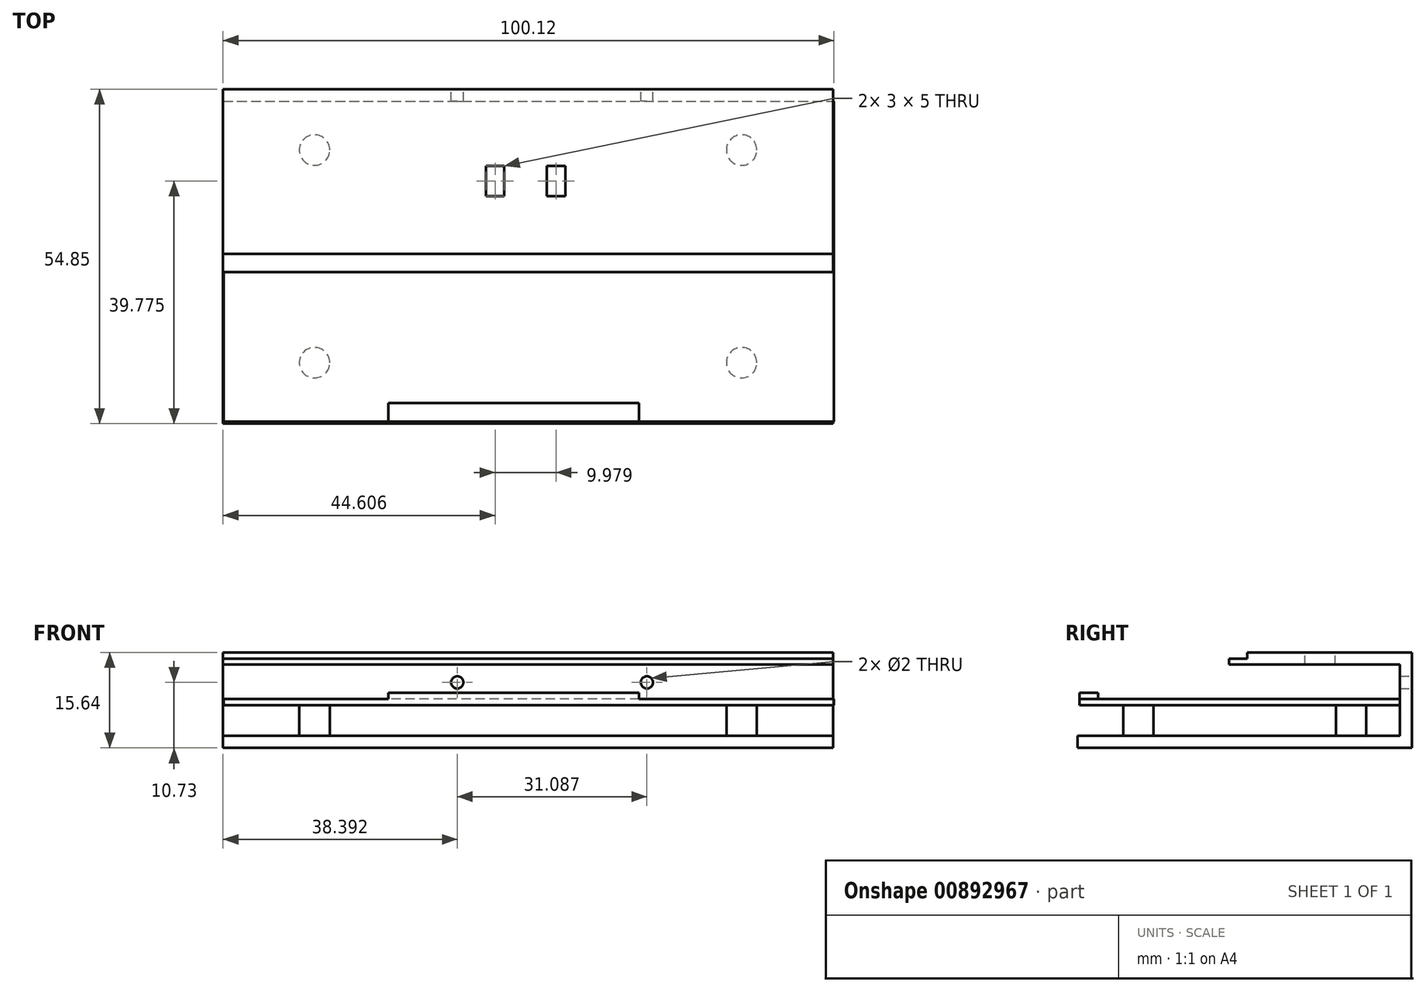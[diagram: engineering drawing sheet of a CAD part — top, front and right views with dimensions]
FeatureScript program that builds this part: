
annotation { "Feature Type Name" : "Feature", "Feature Type Description" : "" }
export const myFeature = defineFeature(function(context is Context, id is Id, definition is map)
    precondition{}
    {
        {
            var Q0;
            Q0=qCreatedBy(makeId("Right.planeOp"),FACE);
            var sketch = newSketch(context, id + "F0", { "sketchPlane" : qUnion([Q0])});
            skLineSegment(sketch, "E0", {"start": v(-52.85, 0) * mm, "end": v(0, 0) * mm});
            skLineSegment(sketch, "E1", {"start": v(0, 0) * mm, "end": v(0, 13.64) * mm});
            skLineSegment(sketch, "E2.0", {"start": v(2, -2) * mm, "end": v(2, 13.64) * mm});
            skLineSegment(sketch, "E2.1", {"start": v(-52.85, -2) * mm, "end": v(2, -2) * mm});
            skLineSegment(sketch, "E3.bottom", {"start": v(-52.85, -2) * mm, "end": v(-52.85, -2) * mm});
            skLineSegment(sketch, "E3.top", {"start": v(-52.85, 0) * mm, "end": v(-52.85, 0) * mm});
            skLineSegment(sketch, "E3.left", {"start": v(-52.85, -2) * mm, "end": v(-52.85, 0) * mm});
            skLineSegment(sketch, "E3.right", {"start": v(-52.85, -2) * mm, "end": v(-52.85, 0) * mm});
            skLineSegment(sketch, "E4.bottom", {"start": v(0, 13.64) * mm, "end": v(2, 13.64) * mm});
            skLineSegment(sketch, "E4.top", {"start": v(0, 13.64) * mm, "end": v(2, 13.64) * mm});
            skLineSegment(sketch, "E4.left", {"start": v(0, 13.64) * mm, "end": v(0, 13.64) * mm});
            skLineSegment(sketch, "E4.right", {"start": v(2, 13.64) * mm, "end": v(2, 13.64) * mm});
            skSolve(sketch);
        }
        {
            var Q0;
            Q0=makeQuery(id+"F0.imprint","IMPRINT",FACE,{"disambiguationData":[TD([[makeQuery(id+"F0.imprint","IMPRINT",EDGE,{"derivedFrom":sQuery(id+"F0.wireOp",EDGE,"E0")}),-1.0]])]});
            extrude(context, id + "F1", {"entities" : qUnion([Q0]), "depth" : 100 * mm, "offsetDistance" : 25 * mm});
        }
        {
            var Q0;
            Q0=makeQuery(id+"F1.opExtrude","SWEPT_FACE",FACE,{"disambiguationData":[OSD([sQuery(id+"F0.wireOp",EDGE,"E1")])]});
            var sketch = newSketch(context, id + "F2", { "sketchPlane" : qUnion([Q0])});
            skLineSegment(sketch, "E5.bottom", {"start": v(0, 13.64) * mm, "end": v(100, 13.64) * mm});
            skLineSegment(sketch, "E5.top", {"start": v(0, 11.64) * mm, "end": v(100, 11.64) * mm});
            skLineSegment(sketch, "E5.left", {"start": v(0, 13.64) * mm, "end": v(0, 11.64) * mm});
            skLineSegment(sketch, "E5.right", {"start": v(100, 13.64) * mm, "end": v(100, 11.64) * mm});
            skSolve(sketch);
        }
        {
            var Q0;
            Q0=makeQuery(id+"F2.imprint","IMPRINT",FACE,{"disambiguationData":[TD([[makeQuery(id+"F2.imprint","IMPRINT",EDGE,{"derivedFrom":sQuery(id+"F2.wireOp",EDGE,"E5.bottom")}),1.0]])]});
            extrude(context, id + "F3", {"entities" : qUnion([Q0]), "operationType" : NewBodyOperationType.ADD, "depth" : 25 * mm, "offsetDistance" : 25 * mm});
        }
        {
            var Q0;
            Q0=makeQuery(id+"F1.opExtrude","SWEPT_FACE",FACE,{"disambiguationData":[OSD([sQuery(id+"F0.wireOp",EDGE,"E0")])]});
            var sketch = newSketch(context, id + "F4", { "sketchPlane" : qUnion([Q0])});
            skCircle(sketch, "E6", {"center": v(15, -42.85) * mm, "radius": 2.5 * mm});
            skCircle(sketch, "E7", {"center": v(85, -42.85) * mm, "radius": 2.5 * mm});
            skCircle(sketch, "E8", {"center": v(15, -8) * mm, "radius": 2.5 * mm});
            skCircle(sketch, "E9", {"center": v(85, -8) * mm, "radius": 2.5 * mm});
            skLineSegment(sketch, "E10", {"start": v(0, -8) * mm, "end": v(100, -8) * mm, "construction": true});
            skLineSegment(sketch, "E11", {"start": v(0, -42.85) * mm, "end": v(100, -42.85) * mm, "construction": true});
            skLineSegment(sketch, "E12", {"start": v(15, 1.66) * mm, "end": v(15, -52.85) * mm, "construction": true});
            skLineSegment(sketch, "E13", {"start": v(85, 2.16) * mm, "end": v(85, -52.85) * mm, "construction": true});
            skSolve(sketch);
        }
        {
            var Q0;
            Q0=makeQuery(id+"F4.imprint","IMPRINT",FACE,{"disambiguationData":[TD([[makeQuery(id+"F4.imprint","IMPRINT",EDGE,{"derivedFrom":sQuery(id+"F4.wireOp",EDGE,"E6")}),1.0]])]});
            extrude(context, id + "F5", {"entities" : qUnion([Q0]), "operationType" : NewBodyOperationType.ADD, "depth" : 5 * mm, "offsetDistance" : 25 * mm});
        }
        {
            var Q0;
            Q0 = qSketchRegion(id + "F4", true);
            extrude(context, id + "F6", {"entities" : qUnion([Q0]), "operationType" : NewBodyOperationType.ADD, "depth" : 5 * mm, "offsetDistance" : 25 * mm});
        }
        {
            var Q0;
            Q0=makeQuery(id+"F3.boolean.opBoolean","MERGE",FACE,{"derivedFrom":[makeQuery(id+"F1.opExtrude","SWEPT_FACE",FACE,{"disambiguationData":[OSD([sQuery(id+"F0.wireOp",EDGE,"E4.top")])]}),makeQuery(id+"F3.opExtrude","SWEPT_FACE",FACE,{"disambiguationData":[OSD([sQuery(id+"F2.wireOp",EDGE,"E5.bottom")])]})]});
            var sketch = newSketch(context, id + "F7", { "sketchPlane" : qUnion([Q0])});
            skLineSegment(sketch, "E14", {"start": v(100, -15.57) * mm, "end": v(0, -15.57) * mm, "construction": true});
            skLineSegment(sketch, "E15", {"start": v(100, -10.57) * mm, "end": v(0, -10.57) * mm, "construction": true});
            skPoint(sketch, "E15.endSnap0", {"position": v(0, -11.5) * mm});
            skLineSegment(sketch, "E16.bottom", {"start": v(56.08, -15.57) * mm, "end": v(53.08, -15.57) * mm});
            skLineSegment(sketch, "E16.top", {"start": v(56.08, -10.57) * mm, "end": v(53.08, -10.57) * mm});
            skLineSegment(sketch, "E16.left", {"start": v(56.08, -15.57) * mm, "end": v(56.08, -10.57) * mm});
            skLineSegment(sketch, "E16.right", {"start": v(53.08, -15.57) * mm, "end": v(53.08, -10.57) * mm});
            skLineSegment(sketch, "E17.bottom", {"start": v(46.1, -15.57) * mm, "end": v(43.1, -15.57) * mm});
            skLineSegment(sketch, "E17.top", {"start": v(46.1, -10.57) * mm, "end": v(43.1, -10.57) * mm});
            skLineSegment(sketch, "E17.left", {"start": v(46.1, -15.57) * mm, "end": v(46.1, -10.57) * mm});
            skLineSegment(sketch, "E17.right", {"start": v(43.1, -15.57) * mm, "end": v(43.1, -10.57) * mm});
            skText(sketch, "E18", { "text": "LED 1", "fontName": "OpenSans-Regular.ttf"});
            skText(sketch, "E19", { "text": "LED 2", "fontName": "OpenSans-Regular.ttf"});
            const initialGuessF7  = {"E18": [0.0504, -0.0212, 1, 0, 0.0029], "E19": [0.0386, -0.00612, 1, 0, 0.00272]};
            skSetInitialGuess(sketch, initialGuessF7);
            skSolve(sketch);
        }
        {
            var Q0;
            Q0=makeQuery(id+"F7.imprint","IMPRINT",FACE,{"disambiguationData":[TD([[makeQuery(id+"F7.imprint","IMPRINT",EDGE,{"derivedFrom":sQuery(id+"F7.wireOp",EDGE,"E16.bottom")}),-1.0]])]});
            var Q1;
            Q1=makeQuery(id+"F7.imprint","IMPRINT",FACE,{"disambiguationData":[TD([[makeQuery(id+"F7.imprint","IMPRINT",EDGE,{"derivedFrom":sQuery(id+"F7.wireOp",EDGE,"E17.bottom")}),-1.0]])]});
            extrude(context, id + "F8", {"entities" : qUnion([Q0, Q1]), "operationType" : NewBodyOperationType.REMOVE, "endBound" : BoundingType.UP_TO_NEXT, "oppositeDirection" : true, "depth" : 25 * mm, "offsetDistance" : 25 * mm});
        }
        {
            var Q0;
            Q0=makeQuery(id+"F3.opExtrude","CAP_FACE",FACE,{"disambiguationData":[OSD([sQuery(id+"F2.wireOp",EDGE,"E5.bottom"),sQuery(id+"F2.wireOp",EDGE,"E5.top"),sQuery(id+"F2.wireOp",EDGE,"E5.left"),sQuery(id+"F2.wireOp",EDGE,"E5.right")])],"isStart":false});
            var sketch = newSketch(context, id + "F9", { "sketchPlane" : qUnion([Q0])});
            skLineSegment(sketch, "E20.bottom", {"start": v(0, 11.64) * mm, "end": v(100, 11.64) * mm});
            skLineSegment(sketch, "E20.top", {"start": v(0, 12.64) * mm, "end": v(100, 12.64) * mm});
            skLineSegment(sketch, "E20.left", {"start": v(0, 11.64) * mm, "end": v(0, 12.64) * mm});
            skLineSegment(sketch, "E20.right", {"start": v(100, 11.64) * mm, "end": v(100, 12.64) * mm});
            skSolve(sketch);
        }
        {
            var Q0;
            Q0=makeQuery(id+"F9.imprint","IMPRINT",FACE,{"disambiguationData":[TD([[makeQuery(id+"F9.imprint","IMPRINT",EDGE,{"derivedFrom":sQuery(id+"F9.wireOp",EDGE,"E20.bottom")}),1.0]])]});
            extrude(context, id + "F10", {"entities" : qUnion([Q0]), "operationType" : NewBodyOperationType.ADD, "depth" : 3 * mm, "offsetDistance" : 25 * mm});
        }
        {
            var Q0;
            Q0=makeQuery(id+"F1.opExtrude","SWEPT_FACE",FACE,{"disambiguationData":[OSD([sQuery(id+"F0.wireOp",EDGE,"E2.0")])]});
            var sketch = newSketch(context, id + "F11", { "sketchPlane" : qUnion([Q0])});
            skCircle(sketch, "E21", {"center": v(-69.48, 8.73) * mm, "radius": 1 * mm});
            skCircle(sketch, "E22", {"center": v(-38.4, 8.73) * mm, "radius": 1 * mm});
            skLineSegment(sketch, "E23", {"start": v(-100, 8.73) * mm, "end": v(0, 8.73) * mm, "construction": true});
            skPoint(sketch, "E23.endSnap0", {"position": v(0, 5.82) * mm});
            skSolve(sketch);
        }
        {
            var Q0;
            Q0 = qSketchRegion(id + "F11", true);
            extrude(context, id + "F12", {"entities" : qUnion([Q0]), "operationType" : NewBodyOperationType.REMOVE, "endBound" : BoundingType.UP_TO_NEXT, "oppositeDirection" : true, "depth" : 25 * mm, "offsetDistance" : 25 * mm});
        }
        {
            var Q0;
            Q0=makeQuery(id+"F5.opExtrude","CAP_FACE",FACE,{"disambiguationData":[OSD([sQuery(id+"F4.wireOp",EDGE,"E6")])],"isStart":false});
            var sketch = newSketch(context, id + "F13", { "sketchPlane" : qUnion([Q0])});
            skLineSegment(sketch, "E24.bottom", {"start": v(0.12, -52.53) * mm, "end": v(100.12, -52.53) * mm});
            skLineSegment(sketch, "E24.top", {"start": v(0.12, 0) * mm, "end": v(100.12, 0) * mm});
            skLineSegment(sketch, "E24.left", {"start": v(0.12, -52.53) * mm, "end": v(0.12, 0) * mm});
            skLineSegment(sketch, "E24.right", {"start": v(100.12, -52.53) * mm, "end": v(100.12, 0) * mm});
            skLineSegment(sketch, "E25.bottom", {"start": v(27.1, -49.48) * mm, "end": v(68.2, -49.48) * mm});
            skLineSegment(sketch, "E25.top", {"start": v(27.1, -52.53) * mm, "end": v(68.2, -52.53) * mm});
            skLineSegment(sketch, "E25.left", {"start": v(27.1, -49.48) * mm, "end": v(27.1, -52.53) * mm});
            skLineSegment(sketch, "E25.right", {"start": v(68.2, -49.48) * mm, "end": v(68.2, -52.53) * mm});
            skSolve(sketch);
        }
        {
            var Q0;
            Q0 = qSketchRegion(id + "F13", true);
            extrude(context, id + "F14", {"entities" : qUnion([Q0]), "operationType" : NewBodyOperationType.ADD, "depth" : 1 * mm, "offsetDistance" : 25 * mm});
        }
        {
            var Q0;
            Q0=makeQuery(id+"F13.imprint","IMPRINT",FACE,{"disambiguationData":[TD([[makeQuery(id+"F13.imprint","IMPRINT",EDGE,{"derivedFrom":sQuery(id+"F13.wireOp",EDGE,"E25.bottom")}),-1.0]])]});
            extrude(context, id + "F15", {"entities" : qUnion([Q0]), "operationType" : NewBodyOperationType.ADD, "depth" : 2 * mm, "offsetDistance" : 25 * mm});
        }
    });
